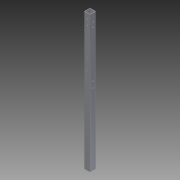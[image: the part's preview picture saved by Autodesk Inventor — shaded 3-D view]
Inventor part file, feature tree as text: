
AUTODESK INVENTOR PART (.ipt)
format: ipt  version: 2013 (Build 170138000, 138)  size: 107,520 bytes
history: native  units: in
note: dims shown in document units (in); Inventor stores cm internally (conversion verified against a paired STEP export)
features: extrude x5, sketch x5, reference x2
ambient origin geometry x8: Origin, YZ Plane, XZ Plane, XY Plane, X Axis, Y Axis, Z Axis, Center Point
bodies: Solid1 (feature_tree)
feature tree (12):
  extrude  "Extrusion1"  Depth=1.0in
  extrude  "Extrusion6"  Depth=23.5in TaperAngle=0.0deg
  extrude  "Extrusion7"  Depth=1.0in TaperAngle=0.0deg
  extrude  "Extrusion8"  Depth=1.5in TaperAngle=0.0deg
  extrude  "Extrusion9"  [1 undecoded]
  sketch  "Sketch1"  dims[d0=1.0in d2=1.0in]
  sketch  "Sketch7"  dims[d3=0.0625in d4=23.5in d5=0.0in]
  sketch  "Sketch8"  dims[d18=1.0in d19=0.0in d20=1.0in d21=0.0in]
  sketch  "Sketch9"  dims[d22=1.0in d23=0.0in d24=1.5in d25=0.0in]
  reference  "Reference15"
  reference  "Reference16"
  sketch  "Sketch10"
note: 1 required parameter value undecoded (feature->parameter linkage not recoverable at this tier; creation-order binding heuristic only, values carry confidence <= 0.55)
